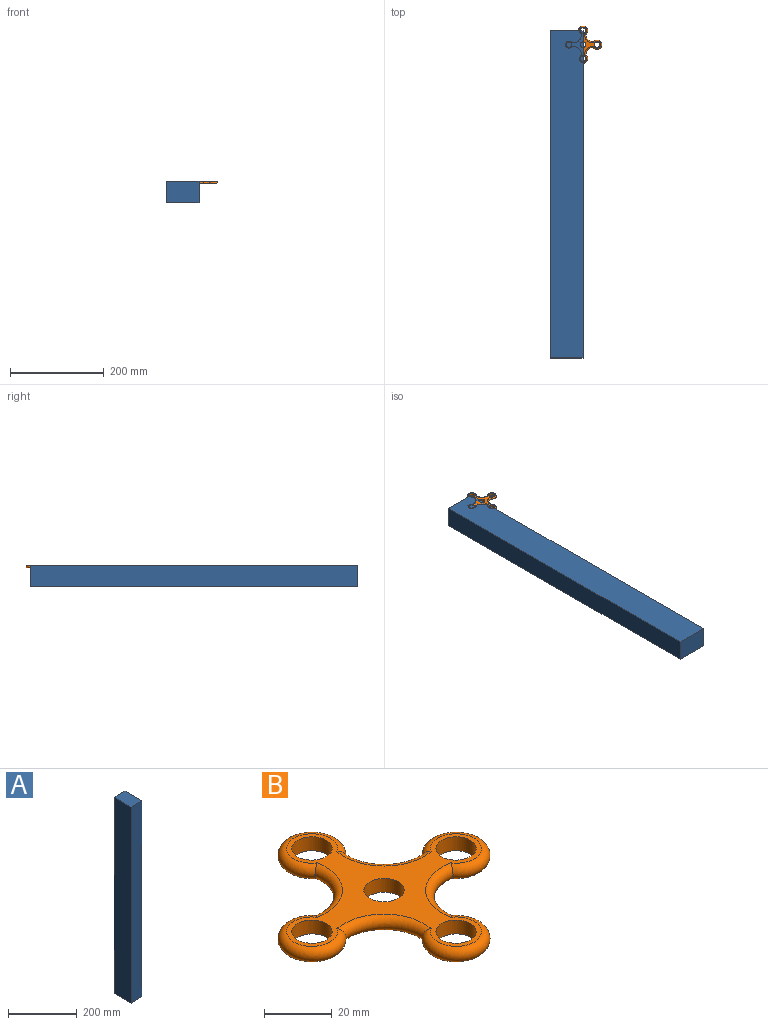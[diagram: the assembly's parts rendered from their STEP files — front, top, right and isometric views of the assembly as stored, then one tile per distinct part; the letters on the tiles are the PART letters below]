
ASSEMBLY  parts=2 mates=1
PART A: 6 faces, bbox 45x70x700 mm
  f0: plane 700x45mm, normal (0,-1,0), area 31500mm2, adj f1,f3,f4,f5
  f1: plane 700x70mm, normal (1,0,0), area 49000mm2, adj f0,f2,f4,f5
  f2: plane 700x45mm, normal (0,1,0), area 31500mm2, adj f1,f3,f4,f5
  f3: plane 700x70mm, normal (-1,0,0), area 49000mm2, adj f0,f2,f4,f5
  f4: plane 70x45mm, normal (0,0,1), area 3150mm2, adj f0,f1,f2,f3
  f5: plane 70x45mm, normal (0,0,-1), area 3150mm2, adj f0,f1,f2,f3
PART B: 15 faces, bbox 81.6x81.6x5 mm
  f0: cylinder r=5.94mm len=11.87mm, axis (0,0,-1), area 186.5mm2, adj f5,f6
  f1: cylinder r=5.94mm len=11.87mm, axis (0,0,-1), area 186.5mm2, adj f5,f6
  f2: cylinder r=5.94mm len=11.87mm, axis (0,0,-1), area 186.5mm2, adj f5,f6
  f3: cylinder r=5.94mm len=11.87mm, axis (0,0,-1), area 186.5mm2, adj f5,f6
  f4: cylinder r=5.94mm len=11.87mm, axis (0,0,-1), area 186.5mm2, adj f5,f6
  f5: plane 75x75mm, normal (0,0,1), area 1028.3mm2, adj f0,f1,f2,f3,f4,f7,f8,f9
  f6: plane 75x75mm, normal (0,0,-1), area 1028.3mm2, adj f0,f1,f2,f3,f4,f7,f8,f9
  f7: torus R=7.5mm, axis (0,0,1), area 354.4mm2, adj f5,f6,f8,f9
  f8: torus R=16.66mm, axis (0,0,1), area 223.4mm2, adj f5,f6,f7,f10
  f9: torus R=16.66mm, axis (0,0,1), area 223.4mm2, adj f5,f6,f7,f11
  f10: torus R=7.5mm, axis (0,0,1), area 354.4mm2, adj f5,f6,f8,f12
  f11: torus R=7.5mm, axis (0,0,1), area 354.4mm2, adj f5,f6,f9,f13
  f12: torus R=16.66mm, axis (0,0,1), area 223.4mm2, adj f5,f6,f10,f14
  f13: torus R=16.66mm, axis (0,0,1), area 223.4mm2, adj f5,f6,f11,f14
  f14: torus R=7.5mm, axis (0,0,1), area 354.4mm2, adj f5,f6,f12,f13
PLACE A rot(axis=(-0.58,0.58,0.58),120deg) t=(-35.07,-320,-17.5)mm
PLACE B at identity
MATE revolute B.f0 <-> A.f3  axis (0,0,1) through (0,30,5)mm
